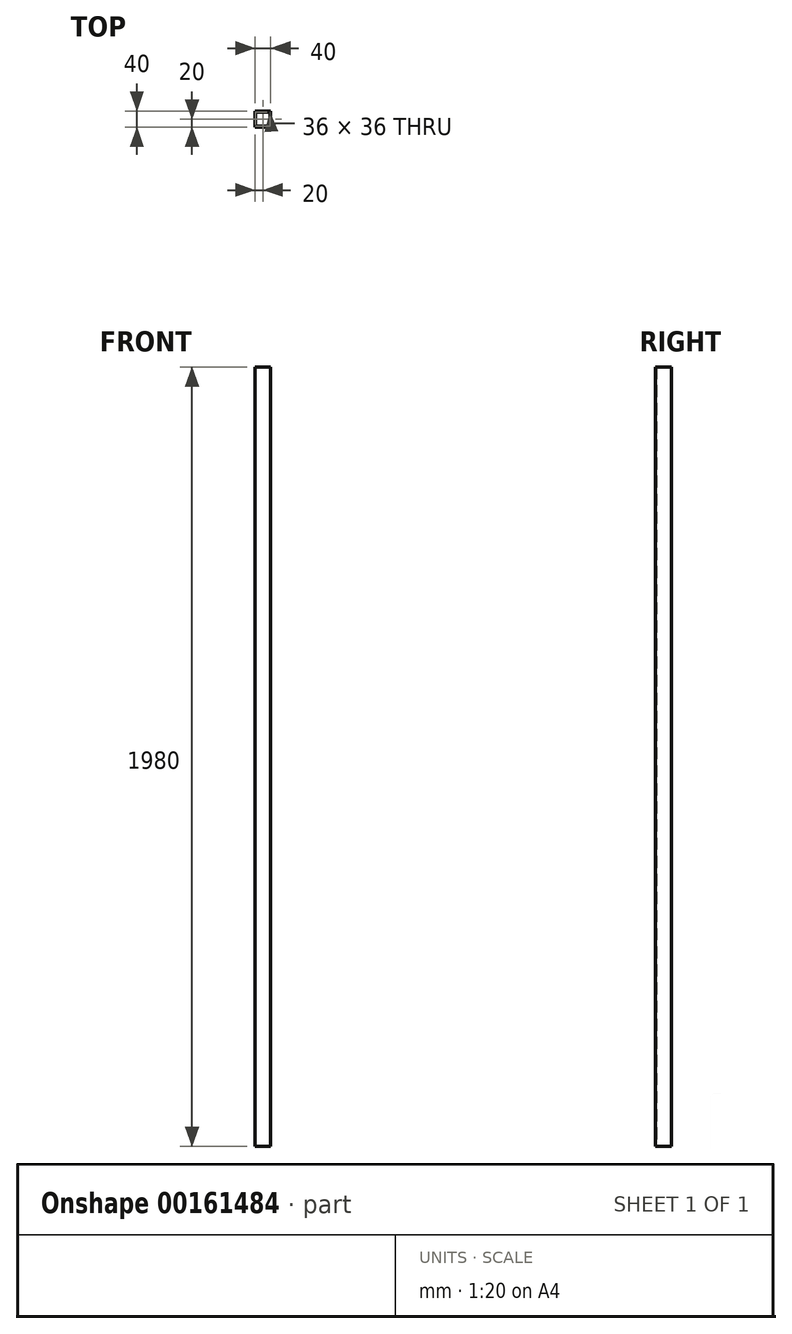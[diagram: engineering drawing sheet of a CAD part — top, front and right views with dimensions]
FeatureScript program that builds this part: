
annotation { "Feature Type Name" : "Feature", "Feature Type Description" : "" }
export const myFeature = defineFeature(function(context is Context, id is Id, definition is map)
    precondition{}
    {
        {
            var Q0;
            Q0=qCreatedBy(makeId("Top.planeOp"),FACE);
            var sketch = newSketch(context, id + "F0", { "sketchPlane" : qUnion([Q0])});
            skLineSegment(sketch, "E0.bottom", {"start": v(20, -20) * mm, "end": v(-20, -20) * mm});
            skLineSegment(sketch, "E0.top", {"start": v(20, 20) * mm, "end": v(-20, 20) * mm});
            skLineSegment(sketch, "E0.left", {"start": v(20, -20) * mm, "end": v(20, 20) * mm});
            skLineSegment(sketch, "E0.right", {"start": v(-20, -20) * mm, "end": v(-20, 20) * mm});
            skPoint(sketch, "E0.middle", {"position": v(0, 0) * mm});
            skLineSegment(sketch, "E1.bottom", {"start": v(18, -18) * mm, "end": v(-18, -18) * mm});
            skLineSegment(sketch, "E1.top", {"start": v(18, 18) * mm, "end": v(-18, 18) * mm});
            skLineSegment(sketch, "E1.left", {"start": v(18, -18) * mm, "end": v(18, 18) * mm});
            skLineSegment(sketch, "E1.right", {"start": v(-18, -18) * mm, "end": v(-18, 18) * mm});
            skSolve(sketch);
        }
        {
            var Q0;
            Q0 = qSketchRegion(id + "F0", true);
            extrude(context, id + "F1", {"entities" : qUnion([Q0]), "depth" : 1980 * mm, "offsetDistance" : 25 * mm});
        }
    });
